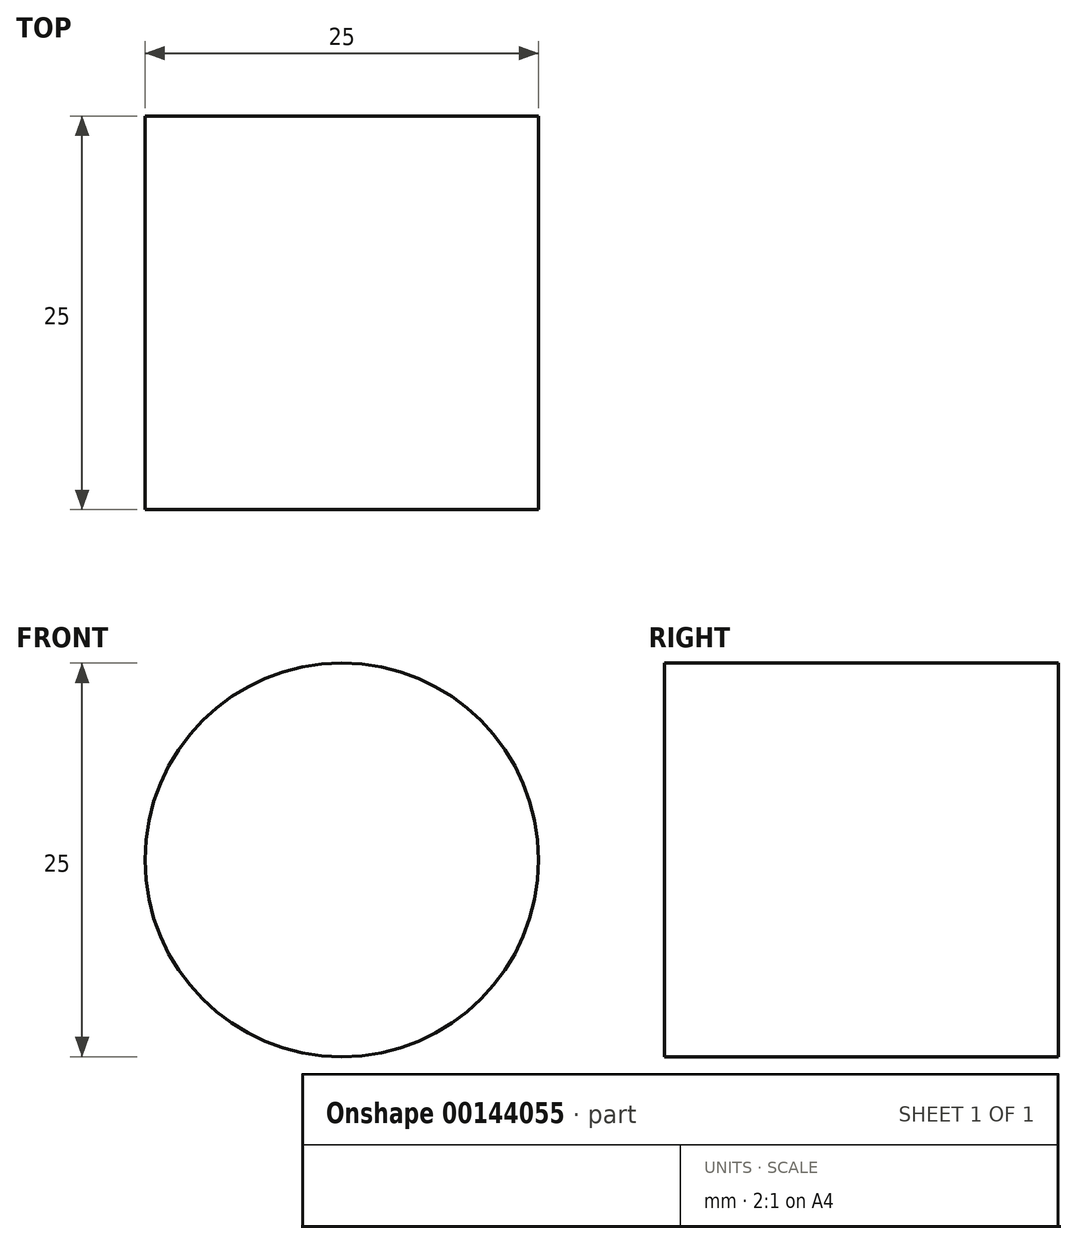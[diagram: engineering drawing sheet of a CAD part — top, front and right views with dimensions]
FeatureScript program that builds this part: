
annotation { "Feature Type Name" : "Feature", "Feature Type Description" : "" }
export const myFeature = defineFeature(function(context is Context, id is Id, definition is map)
    precondition{}
    {
        {
            var Q0;
            Q0=qCreatedBy(makeId("Front.planeOp"),FACE);
            var sketch = newSketch(context, id + "F0", { "sketchPlane" : qUnion([Q0])});
            skCircle(sketch, "E0", {"center": v(0, 0) * mm, "radius": 12.5 * mm});
            skSolve(sketch);
        }
        {
            var Q0;
            Q0 = qSketchRegion(id + "F0", true);
            extrude(context, id + "F1", {"entities" : qUnion([Q0]), "depth" : 25 * mm});
        }
    });
